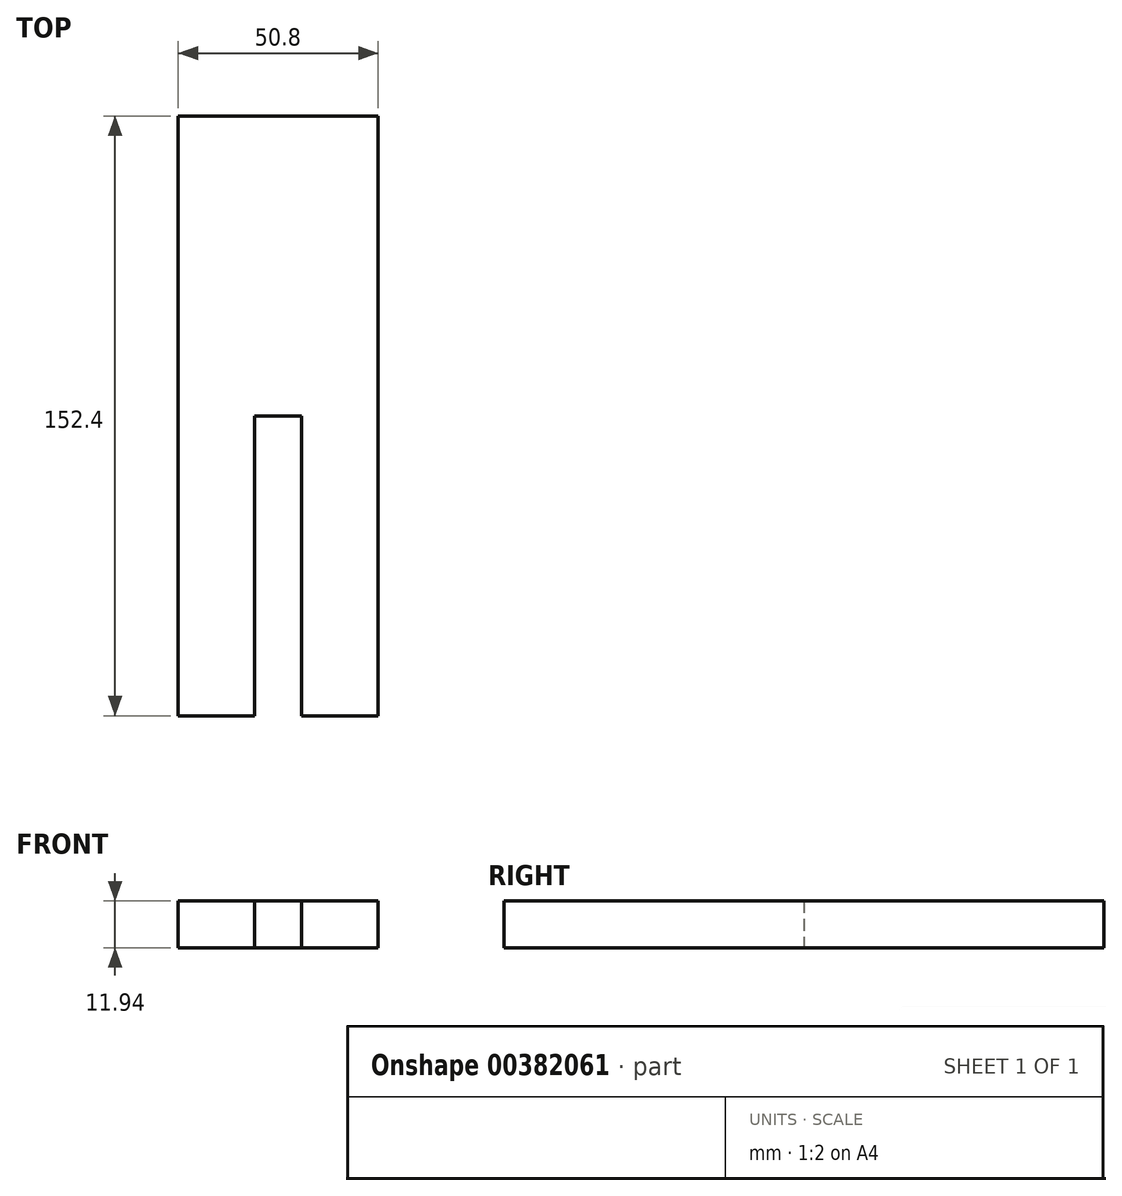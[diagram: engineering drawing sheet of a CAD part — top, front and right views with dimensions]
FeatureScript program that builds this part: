
annotation { "Feature Type Name" : "Feature", "Feature Type Description" : "" }
export const myFeature = defineFeature(function(context is Context, id is Id, definition is map)
    precondition{}
    {
        {
            var Q0;
            Q0=qCreatedBy(makeId("Top.planeOp"),FACE);
            var sketch = newSketch(context, id + "F0", { "sketchPlane" : qUnion([Q0])});
            skLineSegment(sketch, "E0.bottom", {"start": v(-23.42, 0) * mm, "end": v(-4, 0) * mm});
            skLineSegment(sketch, "E0.top", {"start": v(-23.42, 152.4) * mm, "end": v(27.38, 152.4) * mm});
            skLineSegment(sketch, "E0.left", {"start": v(-23.42, 0) * mm, "end": v(-23.42, 152.4) * mm});
            skLineSegment(sketch, "E0.right", {"start": v(27.38, 0) * mm, "end": v(27.38, 152.4) * mm});
            skLineSegment(sketch, "E1", {"start": v(-4, 0) * mm, "end": v(-4, 76.2) * mm});
            skLineSegment(sketch, "E2", {"start": v(-4, 76.2) * mm, "end": v(7.96, 76.2) * mm});
            skLineSegment(sketch, "E3", {"start": v(7.96, 76.2) * mm, "end": v(7.96, 0) * mm});
            skLineSegment(sketch, "E4.trimOffspring", {"start": v(7.96, 0) * mm, "end": v(27.38, 0) * mm});
            skSolve(sketch);
        }
        {
            var Q0;
            Q0=makeQuery(id+"F0.imprint","IMPRINT",FACE,{"disambiguationData":[TD([[makeQuery(id+"F0.imprint","IMPRINT",EDGE,{"derivedFrom":sQuery(id+"F0.wireOp",EDGE,"E0.bottom")}),1.0]])]});
            extrude(context, id + "F1", {"entities" : qUnion([Q0]), "depth" : 11.94 * mm});
        }
    });
